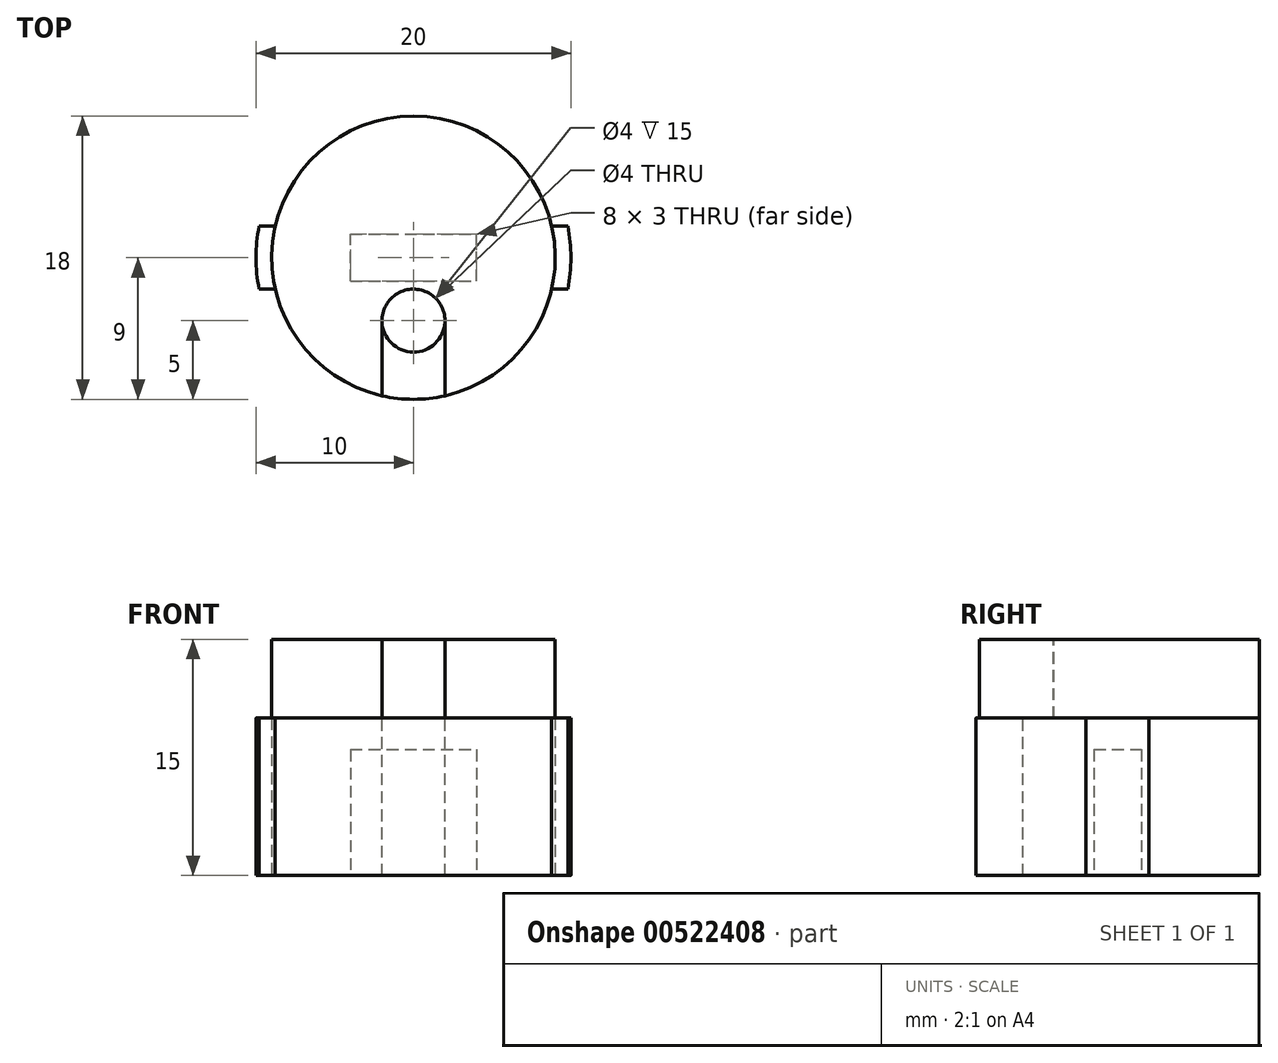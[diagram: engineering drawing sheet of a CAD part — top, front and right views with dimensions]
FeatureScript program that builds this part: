
annotation { "Feature Type Name" : "Feature", "Feature Type Description" : "" }
export const myFeature = defineFeature(function(context is Context, id is Id, definition is map)
    precondition{}
    {
        {
            var Q0;
            Q0=qCreatedBy(makeId("Top.planeOp"),FACE);
            var sketch = newSketch(context, id + "F0", { "sketchPlane" : qUnion([Q0])});
            skCircle(sketch, "E0", {"center": v(0, 0) * mm, "radius": 10 * mm});
            skCircle(sketch, "E1", {"center": v(0, 0) * mm, "radius": 9 * mm});
            skLineSegment(sketch, "E2", {"start": v(-9.8, 2) * mm, "end": v(9.8, 2) * mm});
            skLineSegment(sketch, "E3", {"start": v(-9.8, -2) * mm, "end": v(9.8, -2) * mm});
            skSolve(sketch);
        }
        {
            var Q0;
            {var subQ0=sQuery(id+"F0.wireOp",EDGE,"E2");var subQ1=sQuery(id+"F0.wireOp",EDGE,"E0");var subQ2=makeQuery(id+"F0.imprint","INTERSECT",VERTEX,{"disambiguationData":[OD(0.0)],"derivedFrom":[subQ1,subQ0]});Q0=makeQuery(id+"F0.imprint","IMPRINT",FACE,{"disambiguationData":[TD([[makeQuery(id+"F0.imprint","IMPRINT",EDGE,{"disambiguationData":[TD([[subQ2,-1.0]])],"derivedFrom":subQ1}),1.0]])]});}
            var Q1;
            {var subQ0=sQuery(id+"F0.wireOp",EDGE,"E2");var subQ1=sQuery(id+"F0.wireOp",EDGE,"E0");var subQ2=makeQuery(id+"F0.imprint","INTERSECT",VERTEX,{"disambiguationData":[OD(1.0)],"derivedFrom":[subQ1,subQ0]});Q1=makeQuery(id+"F0.imprint","IMPRINT",FACE,{"disambiguationData":[TD([[makeQuery(id+"F0.imprint","IMPRINT",EDGE,{"disambiguationData":[TD([[subQ2,1.0]])],"derivedFrom":subQ1}),1.0]])]});}
            var Q2;
            {var subQ0=sQuery(id+"F0.wireOp",EDGE,"E2");var subQ1=sQuery(id+"F0.wireOp",EDGE,"E1");var subQ2=makeQuery(id+"F0.imprint","INTERSECT",VERTEX,{"disambiguationData":[OD(0.0)],"derivedFrom":[subQ1,subQ0]});Q2=makeQuery(id+"F0.imprint","IMPRINT",FACE,{"disambiguationData":[TD([[makeQuery(id+"F0.imprint","IMPRINT",EDGE,{"disambiguationData":[TD([[subQ2,1.0]])],"derivedFrom":subQ1}),1.0]])]});}
            var Q3;
            {var subQ0=sQuery(id+"F0.wireOp",EDGE,"E2");var subQ1=sQuery(id+"F0.wireOp",EDGE,"E1");var subQ2=makeQuery(id+"F0.imprint","INTERSECT",VERTEX,{"disambiguationData":[OD(0.0)],"derivedFrom":[subQ1,subQ0]});Q3=makeQuery(id+"F0.imprint","IMPRINT",FACE,{"disambiguationData":[TD([[makeQuery(id+"F0.imprint","IMPRINT",EDGE,{"disambiguationData":[TD([[subQ2,-1.0]])],"derivedFrom":subQ1}),1.0]])]});}
            var Q4;
            {var subQ0=sQuery(id+"F0.wireOp",EDGE,"E3");var subQ1=sQuery(id+"F0.wireOp",EDGE,"E1");var subQ2=makeQuery(id+"F0.imprint","INTERSECT",VERTEX,{"disambiguationData":[OD(0.0)],"derivedFrom":[subQ1,subQ0]});Q4=makeQuery(id+"F0.imprint","IMPRINT",FACE,{"disambiguationData":[TD([[makeQuery(id+"F0.imprint","IMPRINT",EDGE,{"disambiguationData":[TD([[subQ2,-1.0]])],"derivedFrom":subQ1}),1.0]])]});}
            extrude(context, id + "F1", {"entities" : qUnion([Q0, Q1, Q2, Q3, Q4]), "depth" : 10 * mm, "offsetDistance" : 25 * mm});
        }
        {
            var Q0;
            {var subQ0=sQuery(id+"F0.wireOp",EDGE,"E2");var subQ1=sQuery(id+"F0.wireOp",EDGE,"E1");var subQ2=makeQuery(id+"F0.imprint","INTERSECT",VERTEX,{"disambiguationData":[OD(0.0)],"derivedFrom":[subQ1,subQ0]});Q0=makeQuery(id+"F0.imprint","IMPRINT",FACE,{"disambiguationData":[TD([[makeQuery(id+"F0.imprint","IMPRINT",EDGE,{"disambiguationData":[TD([[subQ2,1.0]])],"derivedFrom":subQ1}),1.0]])]});}
            var Q1;
            {var subQ0=sQuery(id+"F0.wireOp",EDGE,"E2");var subQ1=sQuery(id+"F0.wireOp",EDGE,"E1");var subQ2=makeQuery(id+"F0.imprint","INTERSECT",VERTEX,{"disambiguationData":[OD(0.0)],"derivedFrom":[subQ1,subQ0]});Q1=makeQuery(id+"F0.imprint","IMPRINT",FACE,{"disambiguationData":[TD([[makeQuery(id+"F0.imprint","IMPRINT",EDGE,{"disambiguationData":[TD([[subQ2,-1.0]])],"derivedFrom":subQ1}),1.0]])]});}
            var Q2;
            {var subQ0=sQuery(id+"F0.wireOp",EDGE,"E3");var subQ1=sQuery(id+"F0.wireOp",EDGE,"E1");var subQ2=makeQuery(id+"F0.imprint","INTERSECT",VERTEX,{"disambiguationData":[OD(0.0)],"derivedFrom":[subQ1,subQ0]});Q2=makeQuery(id+"F0.imprint","IMPRINT",FACE,{"disambiguationData":[TD([[makeQuery(id+"F0.imprint","IMPRINT",EDGE,{"disambiguationData":[TD([[subQ2,-1.0]])],"derivedFrom":subQ1}),1.0]])]});}
            extrude(context, id + "F2", {"entities" : qUnion([Q0, Q1, Q2]), "depth" : 15 * mm, "offsetDistance" : 25 * mm});
        }
        {
            var Q0;
            {var subQ0=sQuery(id+"F0.wireOp",EDGE,"E2");var subQ1=sQuery(id+"F0.wireOp",EDGE,"E1");var subQ2=makeQuery(id+"F0.imprint","INTERSECT",VERTEX,{"disambiguationData":[OD(0.0)],"derivedFrom":[subQ1,subQ0]});Q0=makeQuery(id+"F0.imprint","IMPRINT",FACE,{"disambiguationData":[TD([[makeQuery(id+"F0.imprint","IMPRINT",EDGE,{"disambiguationData":[TD([[subQ2,-1.0]])],"derivedFrom":subQ1}),1.0]])]});}
            var sketch = newSketch(context, id + "F3", { "sketchPlane" : qUnion([Q0])});
            skLineSegment(sketch, "E4.bottom", {"start": v(-4, -1.5) * mm, "end": v(4, -1.5) * mm});
            skLineSegment(sketch, "E4.top", {"start": v(-4, 1.5) * mm, "end": v(4, 1.5) * mm});
            skLineSegment(sketch, "E4.left", {"start": v(-4, -1.5) * mm, "end": v(-4, 1.5) * mm});
            skLineSegment(sketch, "E4.right", {"start": v(4, -1.5) * mm, "end": v(4, 1.5) * mm});
            skSolve(sketch);
        }
        {
            var Q0;
            Q0=makeQuery(id+"F3.imprint","IMPRINT",FACE,{"disambiguationData":[TD([[makeQuery(id+"F3.imprint","IMPRINT",EDGE,{"derivedFrom":sQuery(id+"F3.wireOp",EDGE,"E4.bottom")}),1.0]])]});
            extrude(context, id + "F4", {"entities" : qUnion([Q0]), "operationType" : NewBodyOperationType.REMOVE, "depth" : 8 * mm, "offsetDistance" : 25 * mm});
        }
        {
            var Q0;
            Q0=makeQuery(id+"F2.opExtrude","CAP_FACE",FACE,{"disambiguationData":[OSD([sQuery(id+"F0.wireOp",EDGE,"E1")])],"isStart":false});
            var sketch = newSketch(context, id + "F5", { "sketchPlane" : qUnion([Q0])});
            skCircle(sketch, "E5", {"center": v(0, -4) * mm, "radius": 2 * mm});
            skSolve(sketch);
        }
        {
            var Q0;
            Q0 = qSketchRegion(id + "F5", true);
            extrude(context, id + "F6", {"entities" : qUnion([Q0]), "operationType" : NewBodyOperationType.REMOVE, "oppositeDirection" : true, "depth" : 25 * mm, "offsetDistance" : 25 * mm});
        }
        {
            var Q0;
            Q0=makeQuery(id+"F2.opExtrude","CAP_FACE",FACE,{"disambiguationData":[OSD([sQuery(id+"F0.wireOp",EDGE,"E1")])],"isStart":false});
            var sketch = newSketch(context, id + "F7", { "sketchPlane" : qUnion([Q0])});
            skLineSegment(sketch, "E6", {"start": v(-2, -4.04) * mm, "end": v(-2, -8.78) * mm});
            skLineSegment(sketch, "E7", {"start": v(2, -3.92) * mm, "end": v(2, -8.78) * mm});
            skSolve(sketch);
        }
        {
            var Q0;
            {var subQ0=sQuery(id+"F7.wireOp",EDGE,"E6");Q0=makeQuery(id+"F7.imprint","IMPRINT",FACE,{"disambiguationData":[TD([[makeQuery(id+"F7.imprint","IMPRINT",EDGE,{"derivedFrom":subQ0}),1.0]])]});}
            extrude(context, id + "F8", {"entities" : qUnion([Q0]), "operationType" : NewBodyOperationType.REMOVE, "oppositeDirection" : true, "depth" : 5 * mm, "offsetDistance" : 25 * mm});
        }
    });
